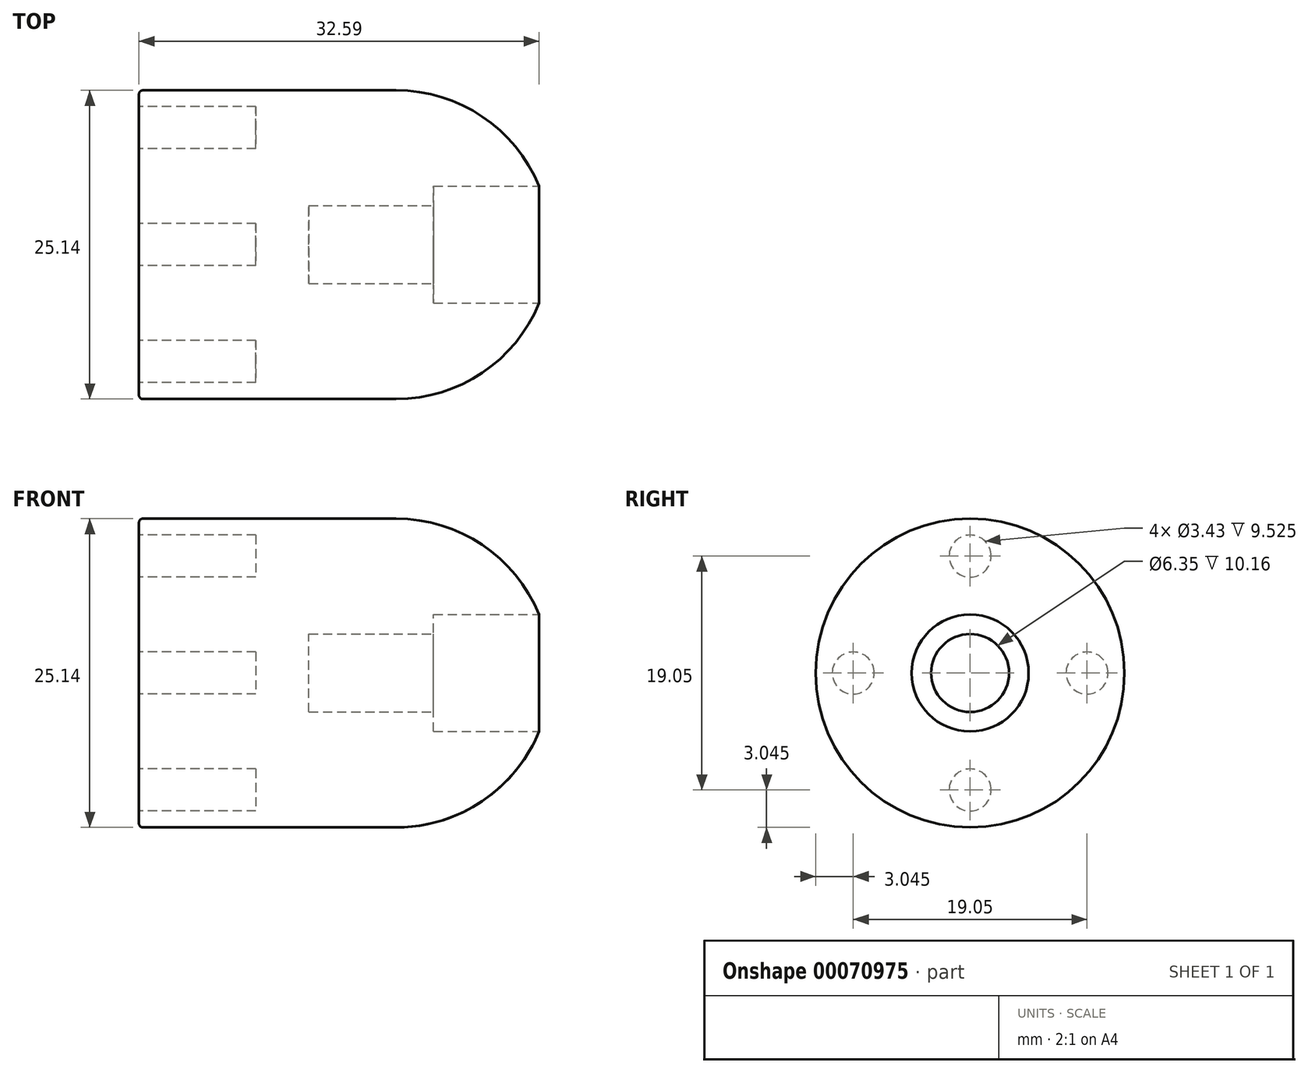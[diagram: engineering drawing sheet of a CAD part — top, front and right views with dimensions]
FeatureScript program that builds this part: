
annotation { "Feature Type Name" : "Feature", "Feature Type Description" : "" }
export const myFeature = defineFeature(function(context is Context, id is Id, definition is map)
    precondition{}
    {
        {
            var Q0;
            Q0=qCreatedBy(makeId("Front.planeOp"),FACE);
            var sketch = newSketch(context, id + "F0", { "sketchPlane" : qUnion([Q0])});
            skLineSegment(sketch, "E0", {"start": v(0, 0) * mm, "end": v(0, 12.57) * mm});
            skLineSegment(sketch, "E1", {"start": v(0, 12.57) * mm, "end": v(20.96, 12.57) * mm});
            skLineSegment(sketch, "E2", {"start": v(32.6, 4.76) * mm, "end": v(24, 4.76) * mm});
            skLineSegment(sketch, "E3", {"start": v(24, 4.76) * mm, "end": v(24, 3.18) * mm});
            skLineSegment(sketch, "E4", {"start": v(24, 3.18) * mm, "end": v(13.84, 3.18) * mm});
            skLineSegment(sketch, "E5", {"start": v(13.84, 3.18) * mm, "end": v(13.84, 0) * mm});
            skLineSegment(sketch, "E6", {"start": v(13.84, 0) * mm, "end": v(0, 0) * mm});
            skArc(sketch, "E7", {"start": v(32.6, 4.76) * mm, "mid": v(27.96, 10.44) * mm, "end": v(20.96, 12.57) * mm});
            skPoint(sketch, "E8.orphan", {"position": v(33.53, 0) * mm});
            skPoint(sketch, "E9.end.orphan", {"position": v(24, 2.38) * mm});
            skPoint(sketch, "E10.orphan", {"position": v(24, 0) * mm});
            skSolve(sketch);
        }
        {
            var Q0;
            Q0=qSketchRegion(id+"F0",true);
            var Q1;
            Q1=sQuery(id+"F0.wireOp",EDGE,"E6");
            revolve(context, id + "F1", {"entities" : qUnion([Q0]), "axis" : qUnion([Q1]), "revolveType" : RevolveType.FULL});
        }
        {
            var Q0;
            Q0=makeQuery(id+"F1.opRevolve","SWEPT_FACE",FACE,{"disambiguationData":[OSD([sQuery(id+"F0.wireOp",EDGE,"E0")])]});
            var sketch = newSketch(context, id + "F2", { "sketchPlane" : qUnion([Q0])});
            skCircle(sketch, "E11", {"center": v(0, 9.53) * mm, "radius": 1.71 * mm});
            skCircle(sketch, "E12", {"center": v(-9.53, 0) * mm, "radius": 1.71 * mm});
            skCircle(sketch, "E13", {"center": v(0, -9.53) * mm, "radius": 1.71 * mm});
            skCircle(sketch, "E14", {"center": v(9.53, 0) * mm, "radius": 1.71 * mm});
            skSolve(sketch);
        }
        {
            var Q0;
            Q0=qSketchRegion(id+"F2",true);
            extrude(context, id + "F3", {"entities" : qUnion([Q0]), "operationType" : NewBodyOperationType.REMOVE, "oppositeDirection" : true, "depth" : 9.52 * mm});
        }
        {
            var Q0;
            Q0=makeQuery(id+"F1.opRevolve","SWEPT_EDGE",EDGE,{"disambiguationData":[OSD([sQuery(id+"F0.wireOp",EDGE,"E0"),sQuery(id+"F0.wireOp",EDGE,"E1")])]});
            fillet(context, id + "F4", {"entities" : qUnion([Q0]), "radius" : 0.3 * mm, "tangentPropagation" : true, "allowEdgeOverflow" : false});
        }
    });
